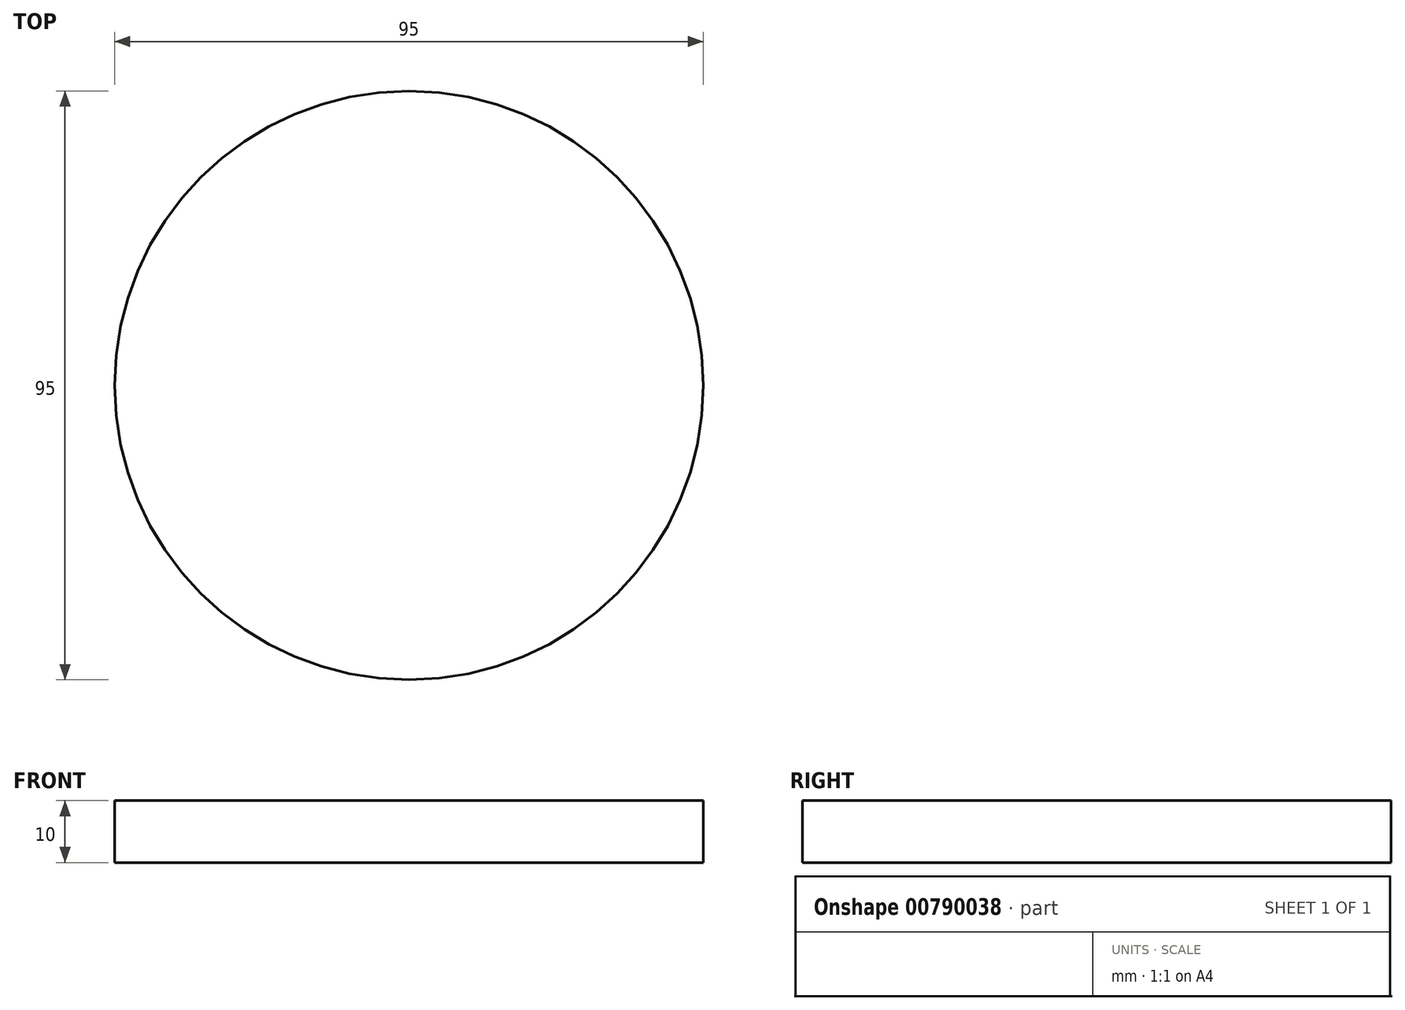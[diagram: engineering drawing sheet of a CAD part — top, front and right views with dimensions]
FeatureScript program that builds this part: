
annotation { "Feature Type Name" : "Feature", "Feature Type Description" : "" }
export const myFeature = defineFeature(function(context is Context, id is Id, definition is map)
    precondition{}
    {
        {
            var Q0;
            Q0=qCreatedBy(makeId("Top.planeOp"),FACE);
            var sketch = newSketch(context, id + "F0", { "sketchPlane" : qUnion([Q0])});
            skCircle(sketch, "E0", {"center": v(0, 0) * mm, "radius": 47.5 * mm});
            skLineSegment(sketch, "E1", {"start": v(0, 59.12) * mm, "end": v(0, -74.03) * mm, "construction": true});
            skLineSegment(sketch, "E2", {"start": v(-79.52, 0) * mm, "end": v(85.22, 0) * mm, "construction": true});
            skSolve(sketch);
        }
        {
            var Q0;
            Q0=qSketchRegion(id+"F0",true);
            extrude(context, id + "F1", {"entities" : qUnion([Q0]), "depth" : 10 * mm, "offsetDistance" : 25 * mm, "symmetric" : true});
        }
        {
            var Q0;
            Q0=qCreatedBy(makeId("Front.planeOp"),FACE);
            cPlane(context, id + "F2", {"entities" : qUnion([Q0]), "cplaneType" : CPlaneType.OFFSET, "offset" : (95 / 2) * mm, "width" : 150 * mm, "height" : 150 * mm});
        }
    });
